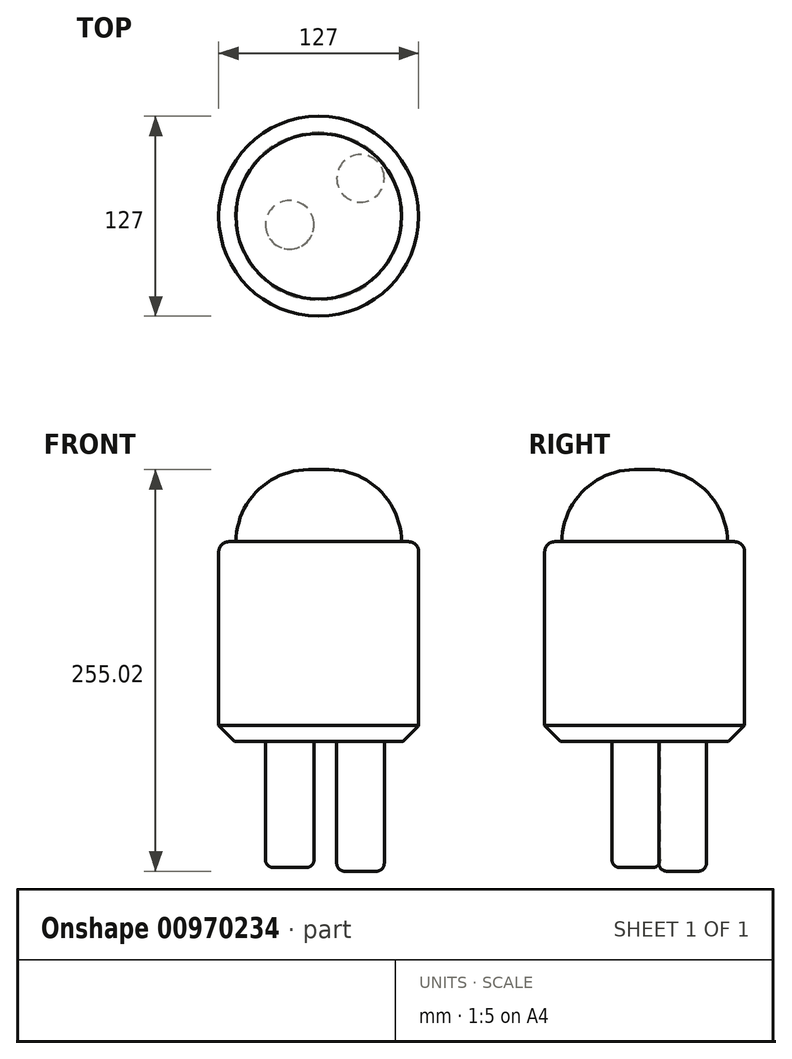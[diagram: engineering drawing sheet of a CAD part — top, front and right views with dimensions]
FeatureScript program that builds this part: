
annotation { "Feature Type Name" : "Feature", "Feature Type Description" : "" }
export const myFeature = defineFeature(function(context is Context, id is Id, definition is map)
    precondition{}
    {
        {
            var Q0;
            Q0=qCreatedBy(makeId("Top.planeOp"),FACE);
            var sketch = newSketch(context, id + "F0", { "sketchPlane" : qUnion([Q0])});
            skCircle(sketch, "E0", {"center": v(0, 0) * mm, "radius": 63.5 * mm});
            skSolve(sketch);
        }
        {
            var Q0;
            Q0=makeQuery(id+"F0.imprint","IMPRINT",FACE,{"disambiguationData":[TD([[makeQuery(id+"F0.imprint","IMPRINT",EDGE,{"derivedFrom":sQuery(id+"F0.wireOp",EDGE,"E0")}),1.0]])]});
            extrude(context, id + "F1", {"entities" : qUnion([Q0]), "depth" : 63.5 * mm, "offsetDistance" : 25.4 * mm, "hasSecondDirection" : true, "secondDirectionOppositeDirection" : true, "secondDirectionDepth" : 63.5 * mm});
        }
        {
            var Q0;
            Q0=makeQuery(id+"F1.opExtrude","CAP_EDGE",EDGE,{"disambiguationData":[OSD([sQuery(id+"F0.wireOp",EDGE,"E0")])],"isStart":true});
            chamfer(context, id + "F2", {"entities" : qUnion([Q0]), "width" : 10.16 * mm, "tangentPropagation" : true});
        }
        {
            var Q0;
            Q0=makeQuery(id+"F1.opExtrude","CAP_EDGE",EDGE,{"disambiguationData":[OSD([sQuery(id+"F0.wireOp",EDGE,"E0")])],"isStart":false});
            fillet(context, id + "F3", {"entities" : qUnion([Q0]), "radius" : 6.35 * mm, "tangentPropagation" : true, "allowEdgeOverflow" : false});
        }
        {
            var Q0;
            Q0=makeQuery(id+"F1.opExtrude","CAP_FACE",FACE,{"disambiguationData":[OSD([sQuery(id+"F0.wireOp",EDGE,"E0")])],"isStart":false});
            var sketch = newSketch(context, id + "F4", { "sketchPlane" : qUnion([Q0])});
            skCircle(sketch, "E1", {"center": v(0, 0) * mm, "radius": 52.56 * mm});
            skSolve(sketch);
        }
        {
            var Q0;
            Q0 = qSketchRegion(id + "F4", true);
            extrude(context, id + "F5", {"entities" : qUnion([Q0]), "operationType" : NewBodyOperationType.ADD, "depth" : 45.72 * mm, "offsetDistance" : 25.4 * mm});
        }
        {
            var Q0;
            Q0=makeQuery(id+"F5.opExtrude","CAP_EDGE",EDGE,{"disambiguationData":[OSD([sQuery(id+"F4.wireOp",EDGE,"E1")])],"isStart":false});
            fillet(context, id + "F6", {"entities" : qUnion([Q0]), "radius" : 46 * mm, "tangentPropagation" : true, "allowEdgeOverflow" : false});
        }
        {
            var Q0;
            Q0=makeQuery(id+"F1.opExtrude","CAP_FACE",FACE,{"disambiguationData":[OSD([sQuery(id+"F0.wireOp",EDGE,"E0")])],"isStart":true});
            var sketch = newSketch(context, id + "F7", { "sketchPlane" : qUnion([Q0])});
            skSolve(sketch);
        }
        {
            var Q0;
            {var subQ0=sQuery(id+"F0.wireOp",EDGE,"E0");Q0=makeQuery(id+"F7.imprint","IMPRINT",FACE,{"disambiguationData":[TD([[makeQuery(id+"F7.imprint","IMPRINT",EDGE,{"derivedFrom":makeQuery(id+"F2.opChamfer","BLEND_EDGE",EDGE,{"blendedFrom":[makeQuery(id+"F1.opExtrude","CAP_EDGE",EDGE,{"disambiguationData":[OSD([subQ0])],"isStart":true}),makeQuery(id+"F1.opExtrude","CAP_FACE",FACE,{"disambiguationData":[OSD([subQ0])],"isStart":true})],"blendedInto":[makeQuery(id+"F1.opExtrude","CAP_FACE",FACE,{"disambiguationData":[OSD([subQ0])],"isStart":true})]})}),1.0]])]});}
            var sketch = newSketch(context, id + "F8", { "sketchPlane" : qUnion([Q0])});
            skCircle(sketch, "E2", {"center": v(26.51, -24.08) * mm, "radius": 15.1 * mm});
            skSolve(sketch);
        }
        {
            var Q0;
            Q0 = qSketchRegion(id + "F8", true);
            extrude(context, id + "F9", {"entities" : qUnion([Q0]), "operationType" : NewBodyOperationType.ADD, "depth" : 82.3 * mm, "offsetDistance" : 25.4 * mm});
        }
        {
            var Q0;
            Q0=makeQuery(id+"F9.opExtrude","CAP_EDGE",EDGE,{"disambiguationData":[OSD([sQuery(id+"F8.wireOp",EDGE,"E2")])],"isStart":false});
            fillet(context, id + "F10", {"entities" : qUnion([Q0]), "radius" : 5.08 * mm, "tangentPropagation" : true, "allowEdgeOverflow" : false});
        }
        {
            var Q0;
            {var subQ0=sQuery(id+"F0.wireOp",EDGE,"E0");Q0=makeQuery(id+"F7.imprint","IMPRINT",FACE,{"disambiguationData":[TD([[makeQuery(id+"F7.imprint","IMPRINT",EDGE,{"derivedFrom":makeQuery(id+"F2.opChamfer","BLEND_EDGE",EDGE,{"blendedFrom":[makeQuery(id+"F1.opExtrude","CAP_EDGE",EDGE,{"disambiguationData":[OSD([subQ0])],"isStart":true}),makeQuery(id+"F1.opExtrude","CAP_FACE",FACE,{"disambiguationData":[OSD([subQ0])],"isStart":true})],"blendedInto":[makeQuery(id+"F1.opExtrude","CAP_FACE",FACE,{"disambiguationData":[OSD([subQ0])],"isStart":true})]})}),1.0]])]});}
            var sketch = newSketch(context, id + "F11", { "sketchPlane" : qUnion([Q0])});
            skCircle(sketch, "E3", {"center": v(-18.45, 5.41) * mm, "radius": 15.4 * mm});
            skSolve(sketch);
        }
        {
            var Q0;
            Q0 = qSketchRegion(id + "F11", true);
            extrude(context, id + "F12", {"entities" : qUnion([Q0]), "operationType" : NewBodyOperationType.ADD, "depth" : 80 * mm, "offsetDistance" : 25.4 * mm});
        }
        {
            var Q0;
            Q0=makeQuery(id+"F12.opExtrude","CAP_EDGE",EDGE,{"disambiguationData":[OSD([sQuery(id+"F11.wireOp",EDGE,"E3")])],"isStart":false});
            fillet(context, id + "F13", {"entities" : qUnion([Q0]), "radius" : 5.08 * mm, "tangentPropagation" : true, "allowEdgeOverflow" : false});
        }
    });
